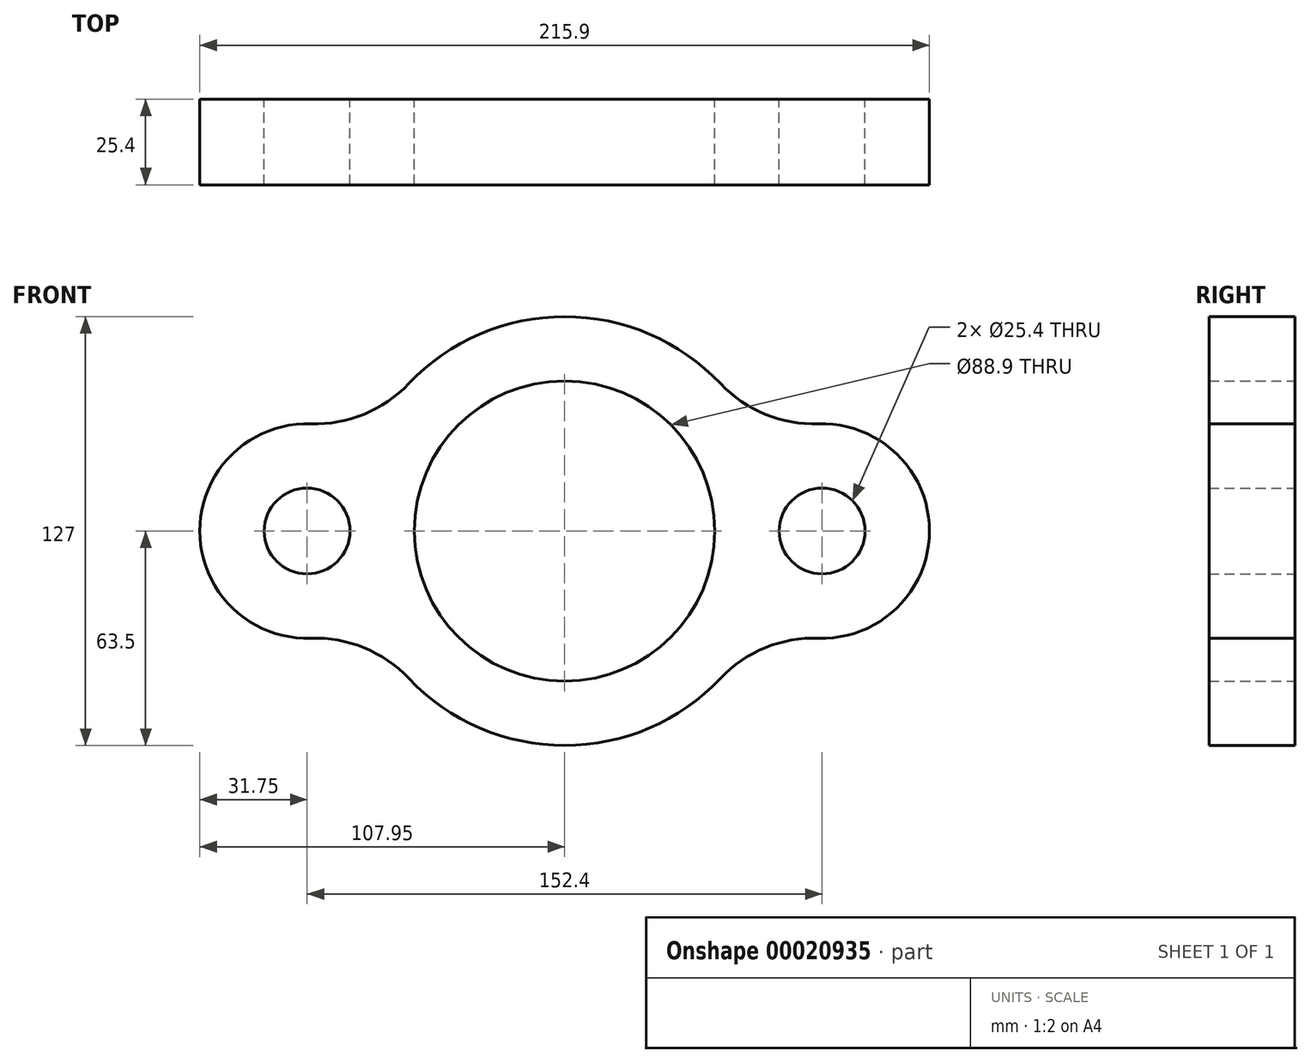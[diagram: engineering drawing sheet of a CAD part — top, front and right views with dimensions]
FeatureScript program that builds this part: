
annotation { "Feature Type Name" : "Feature", "Feature Type Description" : "" }
export const myFeature = defineFeature(function(context is Context, id is Id, definition is map)
    precondition{}
    {
        {
            var Q0;
            Q0=qCreatedBy(makeId("Front.planeOp"),FACE);
            var sketch = newSketch(context, id + "F0", { "sketchPlane" : qUnion([Q0])});
            skCircle(sketch, "E0", {"center": v(0, 0) * mm, "radius": 44.45 * mm});
            skCircle(sketch, "E1", {"center": v(76.2, 0) * mm, "radius": 12.7 * mm});
            skCircle(sketch, "E2", {"center": v(-76.2, 0) * mm, "radius": 12.7 * mm});
            skArc(sketch, "E3", {"start": v(-75.12, 31.73) * mm, "mid": v(-107.95, 0) * mm, "end": v(-75.12, -31.73) * mm});
            skArc(sketch, "E4", {"start": v(75.12, -31.73) * mm, "mid": v(107.95, 0) * mm, "end": v(75.12, 31.73) * mm});
            skArc(sketch, "E5", {"start": v(-44.97, -44.83) * mm, "mid": v(-46.08, -43.61) * mm, "end": v(-47.23, -42.44) * mm});
            skArc(sketch, "E6.trimOffspring", {"start": v(47.86, -41.73) * mm, "mid": v(47.08, -42.57) * mm, "end": v(46.32, -43.43) * mm});
            skArc(sketch, "E7", {"start": v(-75.12, 31.73) * mm, "mid": v(-59.35, 34.56) * mm, "end": v(-46.14, 43.63) * mm});
            skArc(sketch, "E8", {"start": v(46.14, 43.63) * mm, "mid": v(59.35, 34.56) * mm, "end": v(75.12, 31.73) * mm});
            skArc(sketch, "E9", {"start": v(75.12, -31.73) * mm, "mid": v(59.35, -34.56) * mm, "end": v(46.14, -43.63) * mm});
            skArc(sketch, "E10", {"start": v(-46.14, -43.63) * mm, "mid": v(-59.35, -34.56) * mm, "end": v(-75.12, -31.73) * mm});
            skArc(sketch, "E11.trimOffspring", {"start": v(46.14, 43.63) * mm, "mid": v(0, 63.5) * mm, "end": v(-46.14, 43.63) * mm});
            skArc(sketch, "E12.trimOffspring", {"start": v(-47.23, -42.44) * mm, "mid": v(-0.67, -63.5) * mm, "end": v(46.32, -43.43) * mm});
            skSolve(sketch);
        }
        {
            var Q0;
            {var subQ2=sQuery(id+"F0.wireOp",EDGE,"E5");Q0=makeQuery(id+"F0.imprint","IMPRINT",FACE,{"disambiguationData":[TD([[makeQuery(id+"F0.imprint","IMPRINT",EDGE,{"derivedFrom":subQ2}),1.0]])]});}
            var Q1;
            Q1=makeQuery(id+"F0.imprint","IMPRINT",FACE,{"disambiguationData":[TD([[makeQuery(id+"F0.imprint","IMPRINT",EDGE,{"derivedFrom":sQuery(id+"F0.wireOp",EDGE,"E0")}),-1.0]])]});
            extrude(context, id + "F1", {"entities" : qUnion([Q0, Q1]), "depth" : 25.4 * mm});
        }
    });
